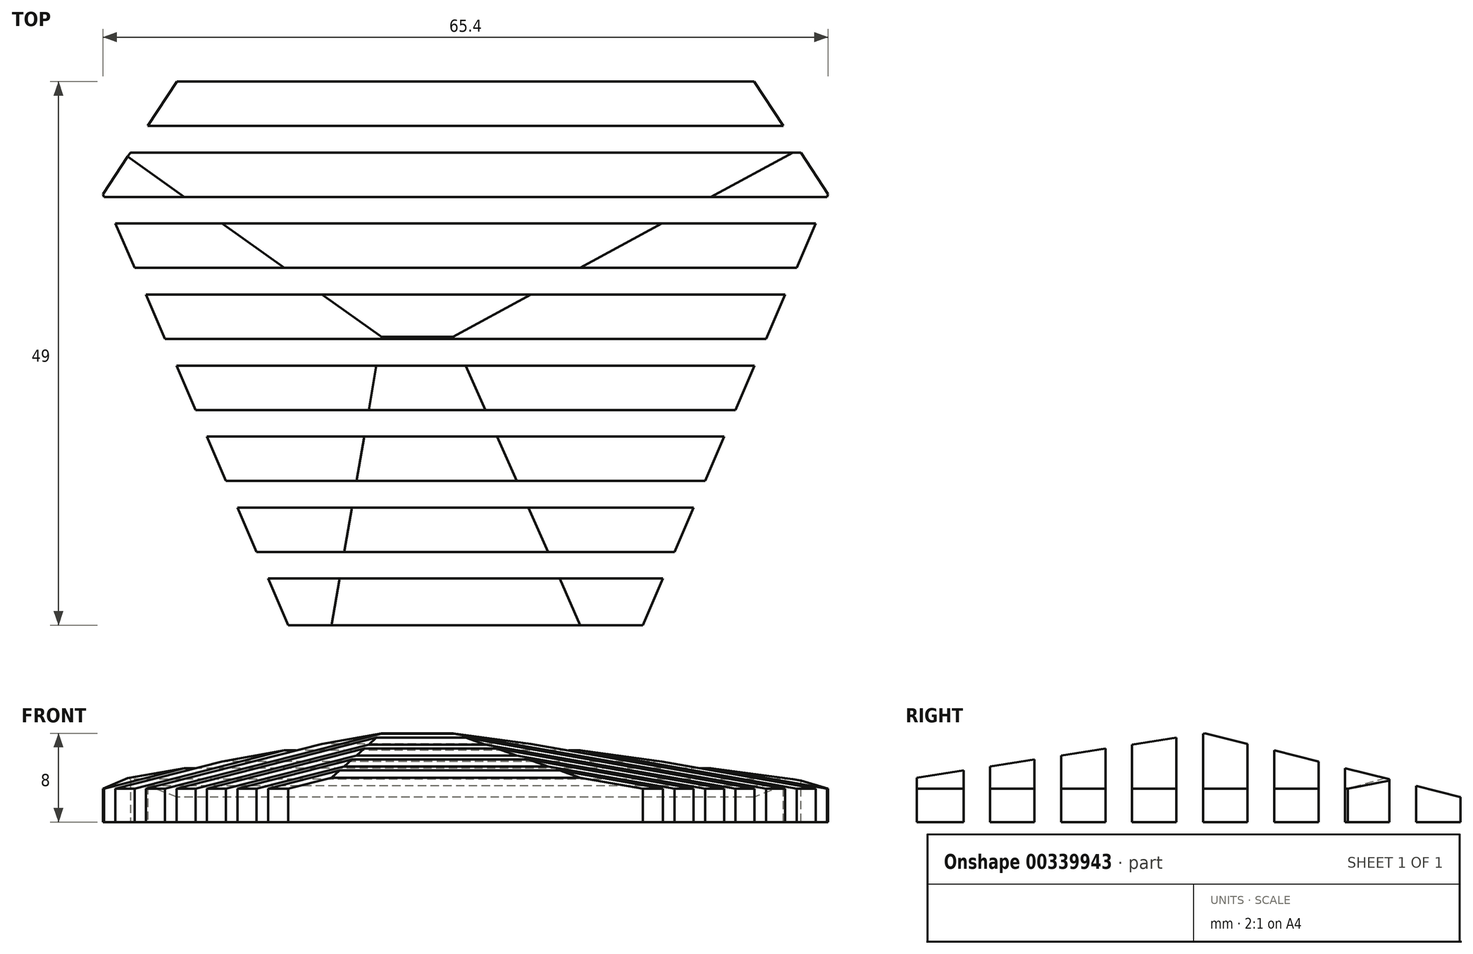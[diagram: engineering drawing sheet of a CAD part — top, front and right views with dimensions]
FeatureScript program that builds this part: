
annotation { "Feature Type Name" : "Feature", "Feature Type Description" : "" }
export const myFeature = defineFeature(function(context is Context, id is Id, definition is map)
    precondition{}
    {
        {
            var Q0;
            Q0=qCreatedBy(makeId("Top.planeOp"),FACE);
            var sketch = newSketch(context, id + "F0", { "sketchPlane" : qUnion([Q0])});
            skLineSegment(sketch, "E0", {"start": v(0, 0) * mm, "end": v(-16, 0) * mm});
            skLineSegment(sketch, "E1", {"start": v(-16, 0) * mm, "end": v(-37.5, 50) * mm});
            skLineSegment(sketch, "E2", {"start": v(-37.5, 50) * mm, "end": v(37.5, 50) * mm});
            skLineSegment(sketch, "E3", {"start": v(37.5, 50) * mm, "end": v(16, 0) * mm});
            skLineSegment(sketch, "E4", {"start": v(16, 0) * mm, "end": v(0, 0) * mm});
            skLineSegment(sketch, "E5", {"start": v(0, 50) * mm, "end": v(0, 0) * mm});
            skSolve(sketch);
        }
        {
            var Q0;
            Q0 = qSketchRegion(id + "F0", true);
            extrude(context, id + "F1", {"entities" : qUnion([Q0]), "depth" : 8 * mm});
        }
        {
            var Q0;
            Q0=makeQuery(id+"F1.opExtrude","CAP_EDGE",EDGE,{"disambiguationData":[OSD([sQuery(id+"F0.wireOp",EDGE,"E1")])],"isStart":false});
            chamfer(context, id + "F2", {"entities" : qUnion([Q0]), "chamferType" : ChamferType.TWO_OFFSETS, "width1" : 5 * mm, "oppositeDirection" : false, "width2" : 18 * mm, "tangentPropagation" : true});
        }
        {
            var Q0;
            Q0=makeQuery(id+"F1.opExtrude","CAP_EDGE",EDGE,{"disambiguationData":[OSD([sQuery(id+"F0.wireOp",EDGE,"E0"),sQuery(id+"F0.wireOp",EDGE,"E4")])],"isStart":false});
            chamfer(context, id + "F3", {"entities" : qUnion([Q0]), "chamferType" : ChamferType.TWO_OFFSETS, "width1" : 4 * mm, "oppositeDirection" : false, "width2" : 26 * mm, "tangentPropagation" : true});
        }
        {
            var Q0;
            Q0=makeQuery(id+"F1.opExtrude","CAP_EDGE",EDGE,{"disambiguationData":[OSD([sQuery(id+"F0.wireOp",EDGE,"E3")])],"isStart":false});
            chamfer(context, id + "F4", {"entities" : qUnion([Q0]), "chamferType" : ChamferType.TWO_OFFSETS, "width1" : 5 * mm, "oppositeDirection" : false, "width2" : 26 * mm, "tangentPropagation" : true});
        }
        {
            var Q0;
            Q0=makeQuery(id+"F1.opExtrude","CAP_EDGE",EDGE,{"disambiguationData":[OSD([sQuery(id+"F0.wireOp",EDGE,"E2")])],"isStart":false});
            chamfer(context, id + "F5", {"entities" : qUnion([Q0]), "chamferType" : ChamferType.TWO_OFFSETS, "width1" : 6 * mm, "oppositeDirection" : false, "width2" : 24 * mm, "tangentPropagation" : true});
        }
        {
            var Q0;
            Q0=makeQuery(id+"F1.opExtrude","SWEPT_EDGE",EDGE,{"disambiguationData":[OSD([sQuery(id+"F0.wireOp",EDGE,"E1"),sQuery(id+"F0.wireOp",EDGE,"E2")])]});
            var Q1;
            Q1=makeQuery(id+"F1.opExtrude","SWEPT_EDGE",EDGE,{"disambiguationData":[OSD([sQuery(id+"F0.wireOp",EDGE,"E2"),sQuery(id+"F0.wireOp",EDGE,"E3")])]});
            chamfer(context, id + "F6", {"entities" : qUnion([Q0, Q1]), "width" : 8 * mm, "tangentPropagation" : true});
        }
        {
            var Q0;
            Q0=qCreatedBy(makeId("Top.planeOp"),FACE);
            cPlane(context, id + "F7", {"entities" : qUnion([Q0]), "cplaneType" : CPlaneType.OFFSET, "offset" : 25 * mm, "width" : 150 * mm, "height" : 150 * mm});
        }
        {
            var Q0;
            Q0=qCreatedBy(id+"F7.planeOp",FACE);
            var sketch = newSketch(context, id + "F8", { "sketchPlane" : qUnion([Q0])});
            skLineSegment(sketch, "E6", {"start": v(0, 0) * mm, "end": v(0, 76.71) * mm});
            skLineSegment(sketch, "E7.bottom", {"start": v(-49.7, 6.6) * mm, "end": v(49.7, 6.6) * mm});
            skLineSegment(sketch, "E7.top", {"start": v(-49.7, 4.2) * mm, "end": v(49.7, 4.2) * mm});
            skLineSegment(sketch, "E7.left", {"start": v(-49.7, 6.6) * mm, "end": v(-49.7, 4.2) * mm});
            skLineSegment(sketch, "E7.right", {"start": v(49.7, 6.6) * mm, "end": v(49.7, 4.2) * mm});
            skPoint(sketch, "E7.middle", {"position": v(0, 5.4) * mm});
            skLineSegment(sketch, "E8.0.1.0", {"start": v(-49.7, 13) * mm, "end": v(49.7, 13) * mm});
            skLineSegment(sketch, "E8.0.1.1", {"start": v(-49.7, 10.6) * mm, "end": v(49.7, 10.6) * mm});
            skLineSegment(sketch, "E8.0.1.2", {"start": v(-49.7, 13) * mm, "end": v(-49.7, 10.6) * mm});
            skLineSegment(sketch, "E8.0.1.3", {"start": v(49.7, 13) * mm, "end": v(49.7, 10.6) * mm});
            skLineSegment(sketch, "E8.0.2.0", {"start": v(-49.7, 19.4) * mm, "end": v(49.7, 19.4) * mm});
            skLineSegment(sketch, "E8.0.2.1", {"start": v(-49.7, 17) * mm, "end": v(49.7, 17) * mm});
            skLineSegment(sketch, "E8.0.2.2", {"start": v(-49.7, 19.4) * mm, "end": v(-49.7, 17) * mm});
            skLineSegment(sketch, "E8.0.2.3", {"start": v(49.7, 19.4) * mm, "end": v(49.7, 17) * mm});
            skLineSegment(sketch, "E8.0.3.0", {"start": v(-49.7, 25.8) * mm, "end": v(49.7, 25.8) * mm});
            skLineSegment(sketch, "E8.0.3.1", {"start": v(-49.7, 23.4) * mm, "end": v(49.7, 23.4) * mm});
            skLineSegment(sketch, "E8.0.3.2", {"start": v(-49.7, 25.8) * mm, "end": v(-49.7, 23.4) * mm});
            skLineSegment(sketch, "E8.0.3.3", {"start": v(49.7, 25.8) * mm, "end": v(49.7, 23.4) * mm});
            skLineSegment(sketch, "E8.0.4.0", {"start": v(-49.7, 32.2) * mm, "end": v(49.7, 32.2) * mm});
            skLineSegment(sketch, "E8.0.4.1", {"start": v(-49.7, 29.8) * mm, "end": v(49.7, 29.8) * mm});
            skLineSegment(sketch, "E8.0.4.2", {"start": v(-49.7, 32.2) * mm, "end": v(-49.7, 29.8) * mm});
            skLineSegment(sketch, "E8.0.4.3", {"start": v(49.7, 32.2) * mm, "end": v(49.7, 29.8) * mm});
            skLineSegment(sketch, "E8.0.5.0", {"start": v(-49.7, 38.6) * mm, "end": v(49.7, 38.6) * mm});
            skLineSegment(sketch, "E8.0.5.1", {"start": v(-49.7, 36.2) * mm, "end": v(49.7, 36.2) * mm});
            skLineSegment(sketch, "E8.0.5.2", {"start": v(-49.7, 38.6) * mm, "end": v(-49.7, 36.2) * mm});
            skLineSegment(sketch, "E8.0.5.3", {"start": v(49.7, 38.6) * mm, "end": v(49.7, 36.2) * mm});
            skLineSegment(sketch, "E8.0.6.0", {"start": v(-49.7, 45) * mm, "end": v(49.7, 45) * mm});
            skLineSegment(sketch, "E8.0.6.1", {"start": v(-49.7, 42.6) * mm, "end": v(49.7, 42.6) * mm});
            skLineSegment(sketch, "E8.0.6.2", {"start": v(-49.7, 45) * mm, "end": v(-49.7, 42.6) * mm});
            skLineSegment(sketch, "E8.0.6.3", {"start": v(49.7, 45) * mm, "end": v(49.7, 42.6) * mm});
            skLineSegment(sketch, "E8.0.7.0", {"start": v(-49.7, 51.4) * mm, "end": v(49.7, 51.4) * mm});
            skLineSegment(sketch, "E8.0.7.1", {"start": v(-49.7, 49) * mm, "end": v(49.7, 49) * mm});
            skLineSegment(sketch, "E8.0.7.2", {"start": v(-49.7, 51.4) * mm, "end": v(-49.7, 49) * mm});
            skLineSegment(sketch, "E8.0.7.3", {"start": v(49.7, 51.4) * mm, "end": v(49.7, 49) * mm});
            skLineSegment(sketch, "E8.direction1", {"start": v(-49.7, 6) * mm, "end": v(-49.8, 6) * mm, "construction": true});
            skLineSegment(sketch, "E8.direction2", {"start": v(-49.7, 6) * mm, "end": v(-49.7, 12.4) * mm, "construction": true});
            skSolve(sketch);
        }
        {
            var Q0;
            {var subQ5=sQuery(id+"F8.wireOp",EDGE,"E8.0.7.2");Q0=makeQuery(id+"F8.imprint","IMPRINT",FACE,{"disambiguationData":[TD([[makeQuery(id+"F8.imprint","IMPRINT",EDGE,{"derivedFrom":subQ5}),1.0]])]});}
            var Q1;
            {var subQ5=sQuery(id+"F8.wireOp",EDGE,"E8.0.7.3");Q1=makeQuery(id+"F8.imprint","IMPRINT",FACE,{"disambiguationData":[TD([[makeQuery(id+"F8.imprint","IMPRINT",EDGE,{"derivedFrom":subQ5}),-1.0]])]});}
            var Q2;
            {var subQ5=sQuery(id+"F8.wireOp",EDGE,"E8.0.6.3");Q2=makeQuery(id+"F8.imprint","IMPRINT",FACE,{"disambiguationData":[TD([[makeQuery(id+"F8.imprint","IMPRINT",EDGE,{"derivedFrom":subQ5}),-1.0]])]});}
            var Q3;
            {var subQ5=sQuery(id+"F8.wireOp",EDGE,"E8.0.5.3");Q3=makeQuery(id+"F8.imprint","IMPRINT",FACE,{"disambiguationData":[TD([[makeQuery(id+"F8.imprint","IMPRINT",EDGE,{"derivedFrom":subQ5}),-1.0]])]});}
            var Q4;
            {var subQ5=sQuery(id+"F8.wireOp",EDGE,"E8.0.4.3");Q4=makeQuery(id+"F8.imprint","IMPRINT",FACE,{"disambiguationData":[TD([[makeQuery(id+"F8.imprint","IMPRINT",EDGE,{"derivedFrom":subQ5}),-1.0]])]});}
            var Q5;
            {var subQ5=sQuery(id+"F8.wireOp",EDGE,"E8.0.3.3");Q5=makeQuery(id+"F8.imprint","IMPRINT",FACE,{"disambiguationData":[TD([[makeQuery(id+"F8.imprint","IMPRINT",EDGE,{"derivedFrom":subQ5}),-1.0]])]});}
            var Q6;
            {var subQ5=sQuery(id+"F8.wireOp",EDGE,"E8.0.2.3");Q6=makeQuery(id+"F8.imprint","IMPRINT",FACE,{"disambiguationData":[TD([[makeQuery(id+"F8.imprint","IMPRINT",EDGE,{"derivedFrom":subQ5}),-1.0]])]});}
            var Q7;
            {var subQ5=sQuery(id+"F8.wireOp",EDGE,"E8.0.1.3");Q7=makeQuery(id+"F8.imprint","IMPRINT",FACE,{"disambiguationData":[TD([[makeQuery(id+"F8.imprint","IMPRINT",EDGE,{"derivedFrom":subQ5}),-1.0]])]});}
            var Q8;
            {var subQ5=sQuery(id+"F8.wireOp",EDGE,"E7.right");Q8=makeQuery(id+"F8.imprint","IMPRINT",FACE,{"disambiguationData":[TD([[makeQuery(id+"F8.imprint","IMPRINT",EDGE,{"derivedFrom":subQ5}),-1.0]])]});}
            var Q9;
            {var subQ5=sQuery(id+"F8.wireOp",EDGE,"E7.left");Q9=makeQuery(id+"F8.imprint","IMPRINT",FACE,{"disambiguationData":[TD([[makeQuery(id+"F8.imprint","IMPRINT",EDGE,{"derivedFrom":subQ5}),1.0]])]});}
            var Q10;
            {var subQ5=sQuery(id+"F8.wireOp",EDGE,"E8.0.1.2");Q10=makeQuery(id+"F8.imprint","IMPRINT",FACE,{"disambiguationData":[TD([[makeQuery(id+"F8.imprint","IMPRINT",EDGE,{"derivedFrom":subQ5}),1.0]])]});}
            var Q11;
            {var subQ5=sQuery(id+"F8.wireOp",EDGE,"E8.0.2.2");Q11=makeQuery(id+"F8.imprint","IMPRINT",FACE,{"disambiguationData":[TD([[makeQuery(id+"F8.imprint","IMPRINT",EDGE,{"derivedFrom":subQ5}),1.0]])]});}
            var Q12;
            {var subQ5=sQuery(id+"F8.wireOp",EDGE,"E8.0.3.2");Q12=makeQuery(id+"F8.imprint","IMPRINT",FACE,{"disambiguationData":[TD([[makeQuery(id+"F8.imprint","IMPRINT",EDGE,{"derivedFrom":subQ5}),1.0]])]});}
            var Q13;
            {var subQ5=sQuery(id+"F8.wireOp",EDGE,"E8.0.4.2");Q13=makeQuery(id+"F8.imprint","IMPRINT",FACE,{"disambiguationData":[TD([[makeQuery(id+"F8.imprint","IMPRINT",EDGE,{"derivedFrom":subQ5}),1.0]])]});}
            var Q14;
            {var subQ5=sQuery(id+"F8.wireOp",EDGE,"E8.0.5.2");Q14=makeQuery(id+"F8.imprint","IMPRINT",FACE,{"disambiguationData":[TD([[makeQuery(id+"F8.imprint","IMPRINT",EDGE,{"derivedFrom":subQ5}),1.0]])]});}
            var Q15;
            {var subQ5=sQuery(id+"F8.wireOp",EDGE,"E8.0.6.2");Q15=makeQuery(id+"F8.imprint","IMPRINT",FACE,{"disambiguationData":[TD([[makeQuery(id+"F8.imprint","IMPRINT",EDGE,{"derivedFrom":subQ5}),1.0]])]});}
            extrude(context, id + "F9", {"entities" : qUnion([Q0, Q1, Q2, Q3, Q4, Q5, Q6, Q7, Q8, Q9, Q10, Q11, Q12, Q13, Q14, Q15]), "operationType" : NewBodyOperationType.REMOVE, "oppositeDirection" : true, "depth" : 36.2 * mm});
        }
    });
